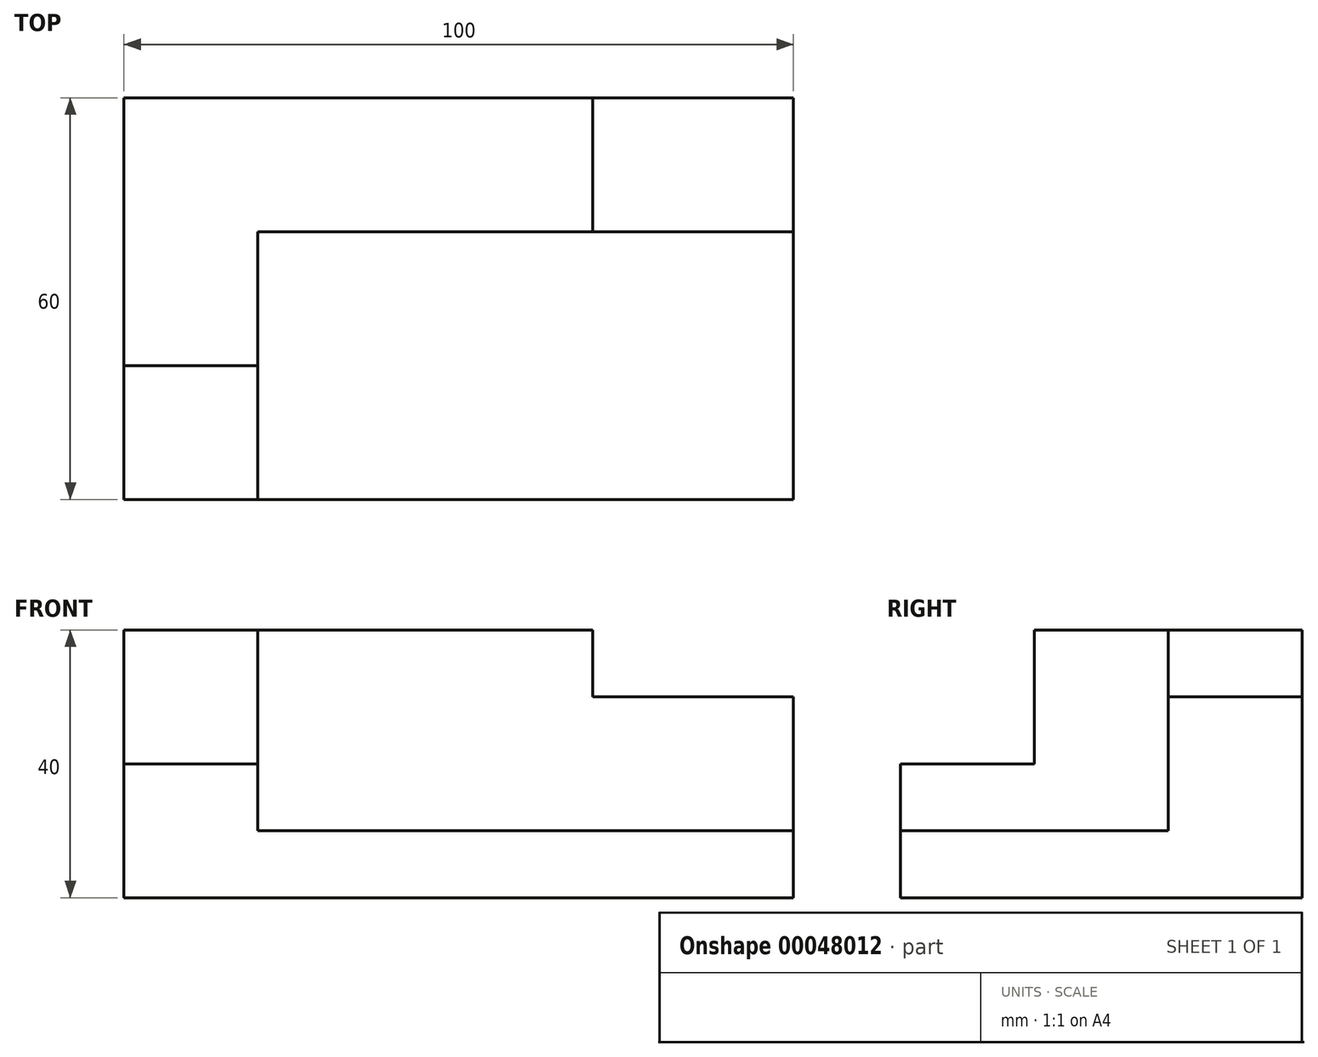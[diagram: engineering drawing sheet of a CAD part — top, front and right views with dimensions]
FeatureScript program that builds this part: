
annotation { "Feature Type Name" : "Feature", "Feature Type Description" : "" }
export const myFeature = defineFeature(function(context is Context, id is Id, definition is map)
    precondition{}
    {
        {
            var Q0;
            Q0=qCreatedBy(makeId("Front.planeOp"),FACE);
            var sketch = newSketch(context, id + "F0", { "sketchPlane" : qUnion([Q0])});
            skLineSegment(sketch, "E0", {"start": v(0, 0) * mm, "end": v(0, 40) * mm});
            skLineSegment(sketch, "E1", {"start": v(0, 40) * mm, "end": v(100, 40) * mm});
            skLineSegment(sketch, "E2", {"start": v(100, 40) * mm, "end": v(100, 0) * mm});
            skLineSegment(sketch, "E3", {"start": v(100, 0) * mm, "end": v(0, 0) * mm});
            skLineSegment(sketch, "E4", {"start": v(70, 40) * mm, "end": v(70, 30) * mm});
            skLineSegment(sketch, "E5", {"start": v(70, 30) * mm, "end": v(100, 30) * mm});
            skLineSegment(sketch, "E6", {"start": v(20, 40) * mm, "end": v(20, 10) * mm});
            skLineSegment(sketch, "E7", {"start": v(20, 10) * mm, "end": v(100, 10) * mm});
            skSolve(sketch);
        }
        {
            var Q0;
            {var subQ2=sQuery(id+"F0.wireOp",EDGE,"E0");Q0=makeQuery(id+"F0.imprint","IMPRINT",FACE,{"disambiguationData":[TD([[makeQuery(id+"F0.imprint","IMPRINT",EDGE,{"derivedFrom":subQ2}),-1.0]])]});}
            var Q1;
            {var subQ4=sQuery(id+"F0.wireOp",EDGE,"E4");Q1=makeQuery(id+"F0.imprint","IMPRINT",FACE,{"disambiguationData":[TD([[makeQuery(id+"F0.imprint","IMPRINT",EDGE,{"derivedFrom":subQ4}),-1.0]])]});}
            extrude(context, id + "F1", {"entities" : qUnion([Q0, Q1]), "oppositeDirection" : true, "depth" : 60 * mm});
        }
        {
            var Q0;
            Q0=makeQuery(id+"F1.opExtrude","CAP_FACE",FACE,{"disambiguationData":[OSD([sQuery(id+"F0.wireOp",EDGE,"E0"),sQuery(id+"F0.wireOp",EDGE,"E1"),sQuery(id+"F0.wireOp",EDGE,"E2"),sQuery(id+"F0.wireOp",EDGE,"E3"),sQuery(id+"F0.wireOp",EDGE,"E4"),sQuery(id+"F0.wireOp",EDGE,"E5")])],"isStart":true});
            var sketch = newSketch(context, id + "F2", { "sketchPlane" : qUnion([Q0])});
            skLineSegment(sketch, "E8", {"start": v(20, 40) * mm, "end": v(20, 10) * mm});
            skLineSegment(sketch, "E9", {"start": v(20, 10) * mm, "end": v(100, 10) * mm});
            skSolve(sketch);
        }
        {
            var Q0;
            {var subQ4=sQuery(id+"F2.wireOp",EDGE,"E8");Q0=makeQuery(id+"F2.imprint","IMPRINT",FACE,{"disambiguationData":[TD([[makeQuery(id+"F2.imprint","IMPRINT",EDGE,{"derivedFrom":subQ4}),1.0]])]});}
            extrude(context, id + "F3", {"entities" : qUnion([Q0]), "operationType" : NewBodyOperationType.REMOVE, "oppositeDirection" : true, "depth" : 40 * mm});
        }
        {
            var Q0;
            Q0=makeQuery(id+"F3.boolean.opBoolean","COPY",FACE,{"derivedFrom":makeQuery(id+"F3.opExtrude","SWEPT_FACE",FACE,{"disambiguationData":[OSD([sQuery(id+"F2.wireOp",EDGE,"E8")])]})});
            var sketch = newSketch(context, id + "F4", { "sketchPlane" : qUnion([Q0])});
            skLineSegment(sketch, "E10", {"start": v(0, 20) * mm, "end": v(20, 20) * mm});
            skLineSegment(sketch, "E11", {"start": v(20, 20) * mm, "end": v(20, 40) * mm});
            skSolve(sketch);
        }
        {
            var Q0;
            {var subQ3=sQuery(id+"F4.wireOp",EDGE,"E10");Q0=makeQuery(id+"F4.imprint","IMPRINT",FACE,{"disambiguationData":[TD([[makeQuery(id+"F4.imprint","IMPRINT",EDGE,{"derivedFrom":subQ3}),1.0]])]});}
            extrude(context, id + "F5", {"entities" : qUnion([Q0]), "operationType" : NewBodyOperationType.REMOVE, "endBound" : BoundingType.UP_TO_NEXT, "oppositeDirection" : true, "depth" : 25 * mm});
        }
    });
